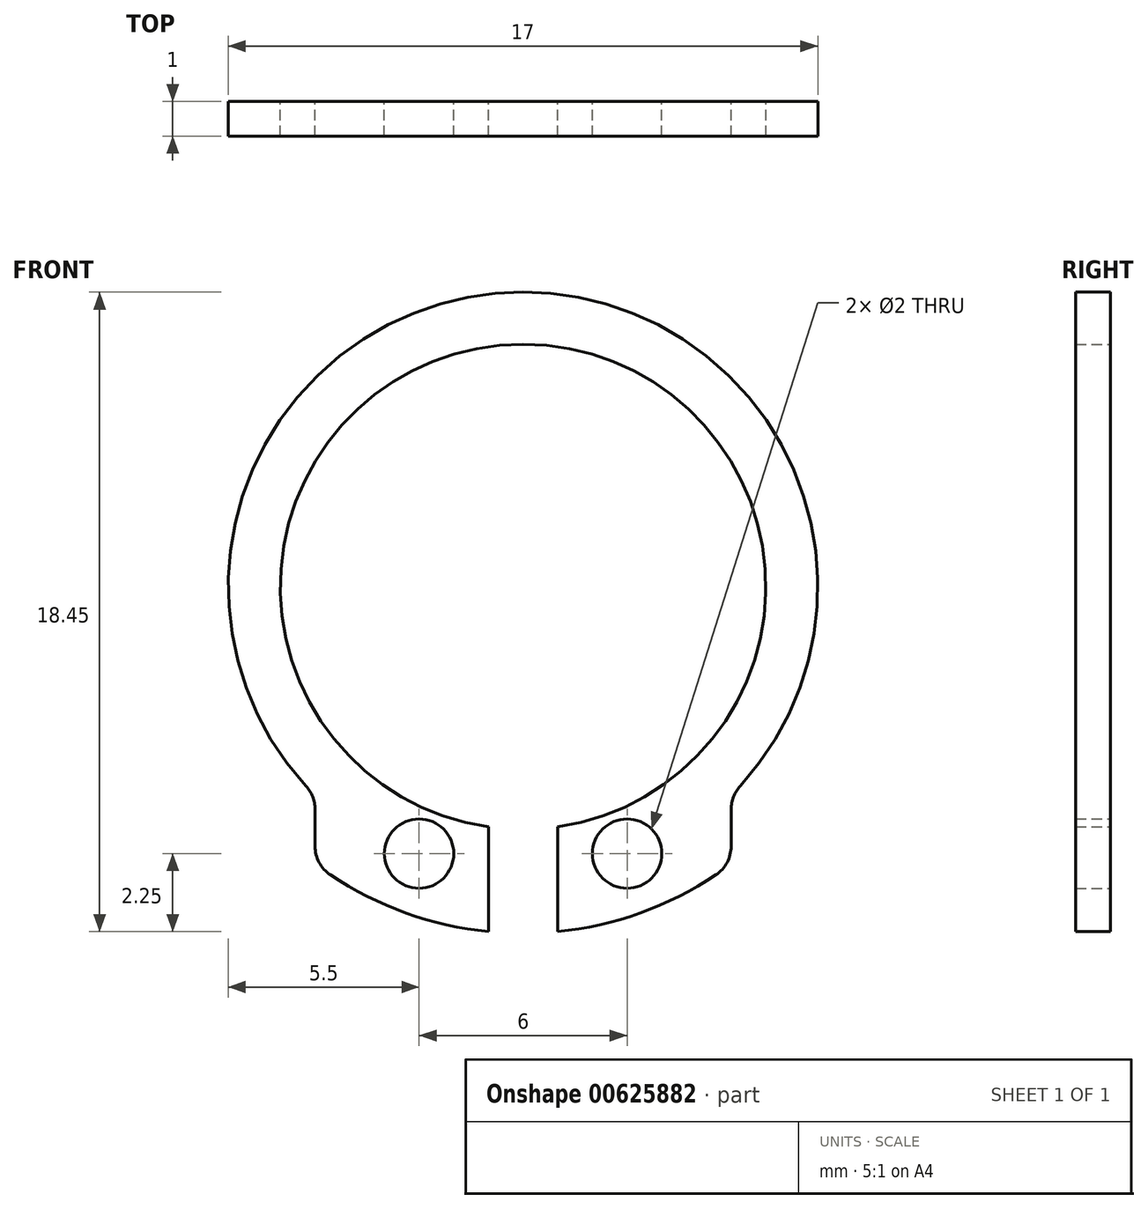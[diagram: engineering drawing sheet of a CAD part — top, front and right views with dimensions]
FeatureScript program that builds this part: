
annotation { "Feature Type Name" : "Feature", "Feature Type Description" : "" }
export const myFeature = defineFeature(function(context is Context, id is Id, definition is map)
    precondition{}
    {
        {
            var Q0;
            Q0=qCreatedBy(makeId("Front.planeOp"),FACE);
            var sketch = newSketch(context, id + "F0", { "sketchPlane" : qUnion([Q0])});
            skArc(sketch, "E0", {"start": v(1, -6.93) * mm, "mid": v(0, 7) * mm, "end": v(-1, -6.93) * mm});
            skArc(sketch, "E1", {"start": v(6.26, -5.75) * mm, "mid": v(0, 8.5) * mm, "end": v(-6.26, -5.75) * mm});
            skArc(sketch, "E2", {"start": v(-5.56, -8.31) * mm, "mid": v(-3.38, -9.41) * mm, "end": v(-1, -9.95) * mm});
            skLineSegment(sketch, "E3", {"start": v(0, 10) * mm, "end": v(0, -10) * mm});
            skLineSegment(sketch, "E4", {"start": v(-1, -6.93) * mm, "end": v(-1, -9.95) * mm});
            skLineSegment(sketch, "E5", {"start": v(-6, -6.42) * mm, "end": v(-6, -7.48) * mm});
            skLineSegment(sketch, "E6.MirrorCS", {"start": v(1, -6.93) * mm, "end": v(1, -9.95) * mm});
            skLineSegment(sketch, "E7.MirrorCS", {"start": v(6, -6.42) * mm, "end": v(6, -7.48) * mm});
            skArc(sketch, "E8.trimOffspring", {"start": v(1, -9.95) * mm, "mid": v(3.38, -9.41) * mm, "end": v(5.56, -8.31) * mm});
            skCircle(sketch, "E9", {"center": v(-3, -7.7) * mm, "radius": 1 * mm});
            skCircle(sketch, "E10.MirrorC", {"center": v(3, -7.7) * mm, "radius": 1 * mm});
            skPoint(sketch, "E11.visualSharp", {"position": v(-6, -6.02) * mm});
            skArc(sketch, "E11.filletArc", {"start": v(-6, -6.42) * mm, "mid": v(-6.07, -6.06) * mm, "end": v(-6.26, -5.75) * mm});
            skPoint(sketch, "E12.visualSharp", {"position": v(-6, -8) * mm});
            skArc(sketch, "E12.filletArc", {"start": v(-6, -7.48) * mm, "mid": v(-5.88, -7.95) * mm, "end": v(-5.56, -8.31) * mm});
            skPoint(sketch, "E13.visualSharp", {"position": v(6, -6.02) * mm});
            skArc(sketch, "E13.filletArc", {"start": v(6.26, -5.75) * mm, "mid": v(6.07, -6.06) * mm, "end": v(6, -6.42) * mm});
            skPoint(sketch, "E14.visualSharp", {"position": v(6, -8) * mm});
            skArc(sketch, "E14.filletArc", {"start": v(5.56, -8.31) * mm, "mid": v(5.88, -7.95) * mm, "end": v(6, -7.48) * mm});
            skSolve(sketch);
        }
        {
            var Q0;
            Q0=makeQuery(id+"F0.imprint","IMPRINT",FACE,{"disambiguationData":[TD([[makeQuery(id+"F0.imprint","IMPRINT",EDGE,{"derivedFrom":sQuery(id+"F0.wireOp",EDGE,"E2")}),1.0]])]});
            var Q1;
            {var subQ0=sQuery(id+"F0.wireOp",EDGE,"E6.MirrorCS");Q1=makeQuery(id+"F0.imprint","IMPRINT",FACE,{"disambiguationData":[TD([[makeQuery(id+"F0.imprint","IMPRINT",EDGE,{"derivedFrom":subQ0}),1.0]])]});}
            extrude(context, id + "F1", {"entities" : qUnion([Q0, Q1]), "depth" : 1 * mm, "offsetDistance" : 25 * mm});
        }
    });
